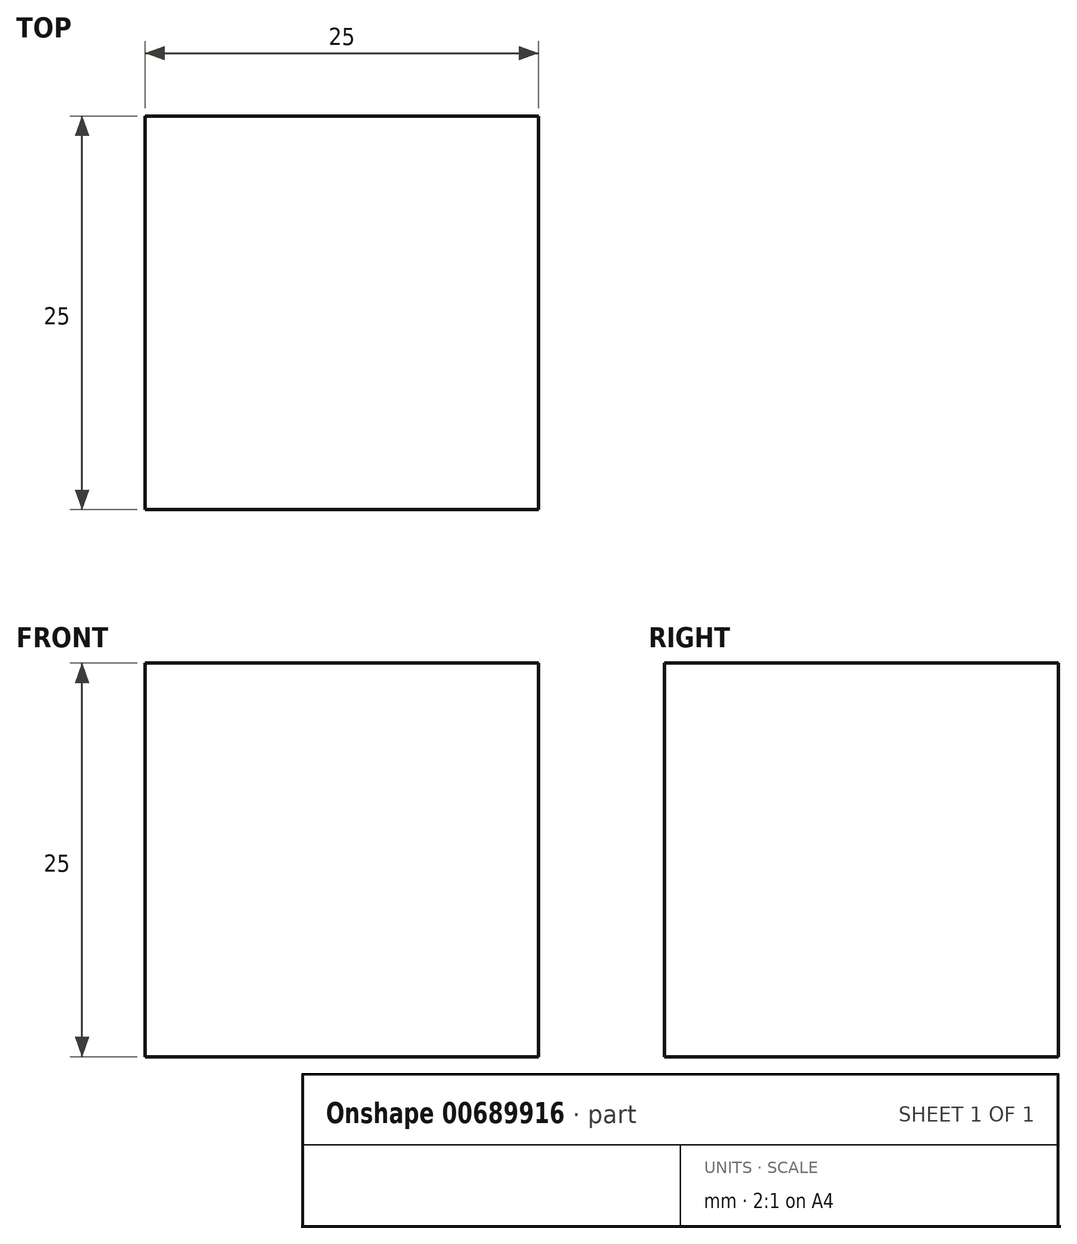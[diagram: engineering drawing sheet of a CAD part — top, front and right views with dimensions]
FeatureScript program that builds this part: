
annotation { "Feature Type Name" : "Feature", "Feature Type Description" : "" }
export const myFeature = defineFeature(function(context is Context, id is Id, definition is map)
    precondition{}
    {
        {
            var Q0;
            Q0=qCreatedBy(makeId("Top.planeOp"),FACE);
            var sketch = newSketch(context, id + "F0", { "sketchPlane" : qUnion([Q0])});
            skLineSegment(sketch, "E0.bottom", {"start": v(-0.1, 11.24) * mm, "end": v(-25.1, 11.24) * mm});
            skLineSegment(sketch, "E0.top", {"start": v(-0.1, 36.24) * mm, "end": v(-25.1, 36.24) * mm});
            skLineSegment(sketch, "E0.left", {"start": v(-0.1, 11.24) * mm, "end": v(-0.1, 36.24) * mm});
            skLineSegment(sketch, "E0.right", {"start": v(-25.1, 11.24) * mm, "end": v(-25.1, 36.24) * mm});
            skPoint(sketch, "E0.middle", {"position": v(-12.6, 23.74) * mm});
            skSolve(sketch);
        }
        {
            var Q0;
            Q0=makeQuery(id+"F0.imprint","IMPRINT",FACE,{"disambiguationData":[TD([[makeQuery(id+"F0.imprint","IMPRINT",EDGE,{"derivedFrom":sQuery(id+"F0.wireOp",EDGE,"E0.bottom")}),-1.0]])]});
            extrude(context, id + "F1", {"entities" : qUnion([Q0]), "depth" : 25 * mm, "offsetDistance" : 25 * mm});
        }
    });
